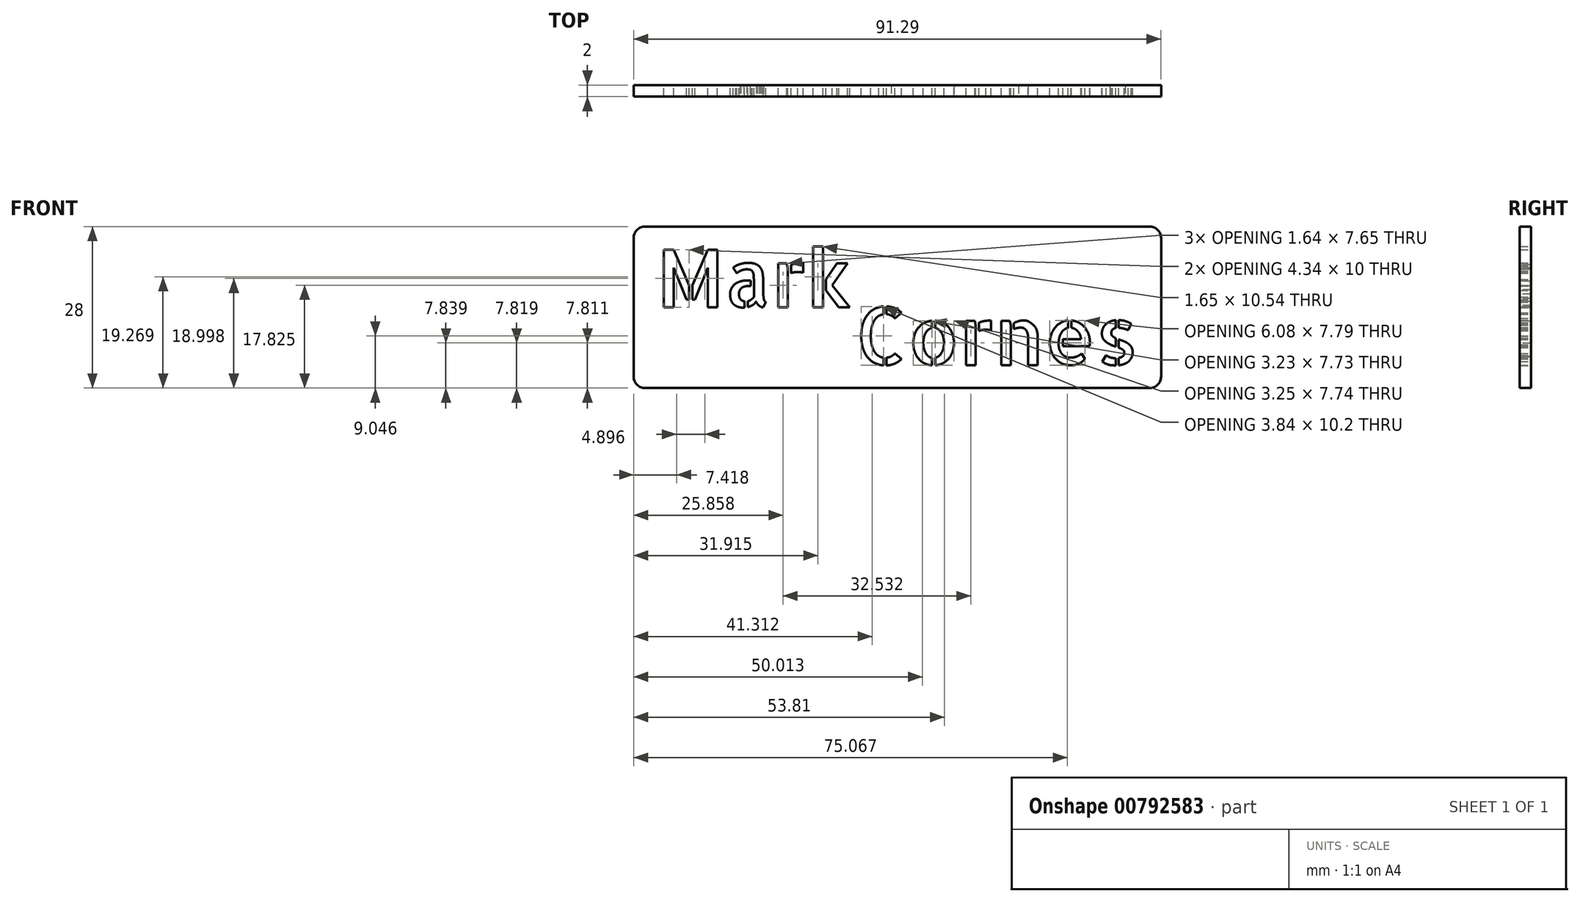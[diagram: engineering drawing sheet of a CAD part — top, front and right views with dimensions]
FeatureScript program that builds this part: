
annotation { "Feature Type Name" : "Feature", "Feature Type Description" : "" }
export const myFeature = defineFeature(function(context is Context, id is Id, definition is map)
    precondition{}
    {
        {
            var Q0;
            Q0=qCreatedBy(makeId("Front.planeOp"),FACE);
            var sketch = newSketch(context, id + "F0", { "sketchPlane" : qUnion([Q0])});
            skText(sketch, "E0", { "text": "Cornes", "fontName": "AllertaStencil-Regular.ttf"});
            skText(sketch, "E1", { "text": "Mark", "fontName": "AllertaStencil-Regular.ttf"});
            skLineSegment(sketch, "E2.bottom", {"start": v(-36.32, 14) * mm, "end": v(50.97, 14) * mm});
            skLineSegment(sketch, "E2.top", {"start": v(-36.32, -14) * mm, "end": v(50.97, -14) * mm});
            skLineSegment(sketch, "E2.left", {"start": v(-38.32, 12) * mm, "end": v(-38.32, -12) * mm});
            skLineSegment(sketch, "E2.right", {"start": v(52.97, 12) * mm, "end": v(52.97, -12) * mm});
            skPoint(sketch, "E3.visualSharp", {"position": v(-38.32, 14) * mm});
            skArc(sketch, "E3.filletArc", {"start": v(-36.32, 14) * mm, "mid": v(-37.74, 13.41) * mm, "end": v(-38.32, 12) * mm});
            skPoint(sketch, "E4.visualSharp", {"position": v(52.97, -14) * mm});
            skArc(sketch, "E4.filletArc", {"start": v(50.97, -14) * mm, "mid": v(52.39, -13.41) * mm, "end": v(52.97, -12) * mm});
            skPoint(sketch, "E5.visualSharp", {"position": v(52.97, 14) * mm});
            skArc(sketch, "E5.filletArc", {"start": v(52.97, 12) * mm, "mid": v(52.39, 13.41) * mm, "end": v(50.97, 14) * mm});
            skPoint(sketch, "E6.visualSharp", {"position": v(-38.32, -14) * mm});
            skArc(sketch, "E6.filletArc", {"start": v(-38.32, -12) * mm, "mid": v(-37.74, -13.41) * mm, "end": v(-36.32, -14) * mm});
            const initialGuessF0  = {"E0": [0, -0.01, 1, 0, 0.01], "E1": [-0.03432, 0, 1, 0, 0.01]};
            skSetInitialGuess(sketch, initialGuessF0);
            skSolve(sketch);
        }
        {
            var Q0;
            Q0 = qSketchRegion(id + "F0", true);
            extrude(context, id + "F1", {"entities" : qUnion([Q0]), "depth" : 2 * mm, "offsetDistance" : 25 * mm});
        }
    });
